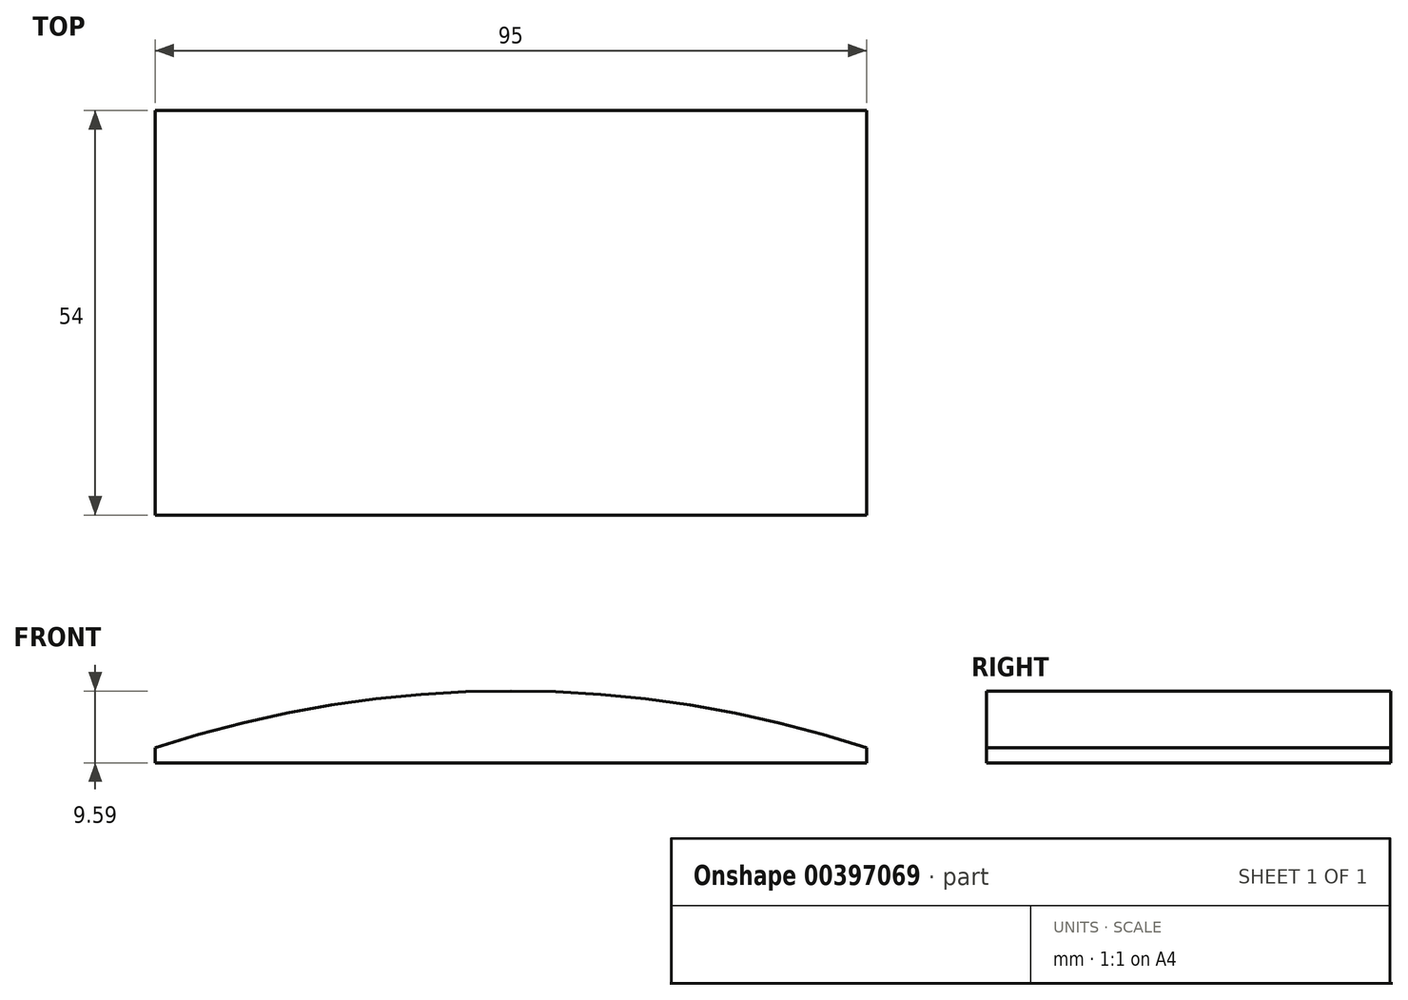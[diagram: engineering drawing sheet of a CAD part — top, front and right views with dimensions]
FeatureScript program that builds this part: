
annotation { "Feature Type Name" : "Feature", "Feature Type Description" : "" }
export const myFeature = defineFeature(function(context is Context, id is Id, definition is map)
    precondition{}
    {
        {
            var Q0;
            Q0=qCreatedBy(makeId("Top.planeOp"),FACE);
            var sketch = newSketch(context, id + "F0", { "sketchPlane" : qUnion([Q0])});
            skLineSegment(sketch, "E0.bottom", {"start": v(-47.5, 27) * mm, "end": v(47.5, 27) * mm});
            skLineSegment(sketch, "E0.top", {"start": v(-47.5, -27) * mm, "end": v(47.5, -27) * mm});
            skLineSegment(sketch, "E0.left", {"start": v(-47.5, 27) * mm, "end": v(-47.5, -27) * mm});
            skLineSegment(sketch, "E0.right", {"start": v(47.5, 27) * mm, "end": v(47.5, -27) * mm});
            skSolve(sketch);
        }
        {
            var Q0;
            Q0 = qSketchRegion(id + "F0", true);
            extrude(context, id + "F1", {"entities" : qUnion([Q0]), "depth" : 2 * mm});
        }
        {
            var Q0;
            Q0=makeQuery(id+"F1.opExtrude","SWEPT_FACE",FACE,{"disambiguationData":[OSD([sQuery(id+"F0.wireOp",EDGE,"E0.top")])]});
            var sketch = newSketch(context, id + "F2", { "sketchPlane" : qUnion([Q0])});
            skArc(sketch, "E1", {"start": v(47.5, 2) * mm, "mid": v(0, 9.6) * mm, "end": v(-47.5, 2) * mm});
            skLineSegment(sketch, "E2", {"start": v(-47.5, 2) * mm, "end": v(47.5, 2) * mm});
            skSolve(sketch);
        }
        {
            var Q0;
            Q0 = qSketchRegion(id + "F2", true);
            extrude(context, id + "F3", {"entities" : qUnion([Q0]), "operationType" : NewBodyOperationType.ADD, "oppositeDirection" : true, "depth" : 54 * mm});
        }
    });
